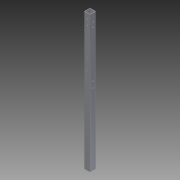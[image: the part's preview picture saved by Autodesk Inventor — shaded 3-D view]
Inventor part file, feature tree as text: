
AUTODESK INVENTOR PART (.ipt)
format: ipt  version: 2013 (Build 170138000, 138)  size: 106,496 bytes
history: native  units: in
note: dims shown in document units (in); Inventor stores cm internally (conversion verified against a paired STEP export)
features: extrude x5, sketch x5, reference x2
ambient origin geometry x8: Origin, YZ Plane, XZ Plane, XY Plane, X Axis, Y Axis, Z Axis, Center Point
bodies: Solid1 (feature_tree)
feature tree (12):
  extrude  "Extrusion1"  Depth=1.0in
  extrude  "Extrusion6"  Depth=23.5in TaperAngle=0.0deg
  extrude  "Extrusion7"  Depth=1.0in TaperAngle=0.0deg
  extrude  "Extrusion8"  Depth=1.5in TaperAngle=0.0deg
  extrude  "Extrusion9"  [1 undecoded]
  sketch  "Sketch1"  dims[d0=1.0in d2=1.0in]
  sketch  "Sketch7"  dims[d3=0.0625in d4=23.5in d5=0.0in]
  sketch  "Sketch8"  dims[d18=1.0in d19=0.0in d20=1.0in d21=0.0in]
  sketch  "Sketch9"  dims[d22=1.0in d23=0.0in d24=1.5in d25=0.0in]
  reference  "Reference15"
  reference  "Reference16"
  sketch  "Sketch10"
note: 1 required parameter value undecoded (feature->parameter linkage not recoverable at this tier; creation-order binding heuristic only, values carry confidence <= 0.55)
